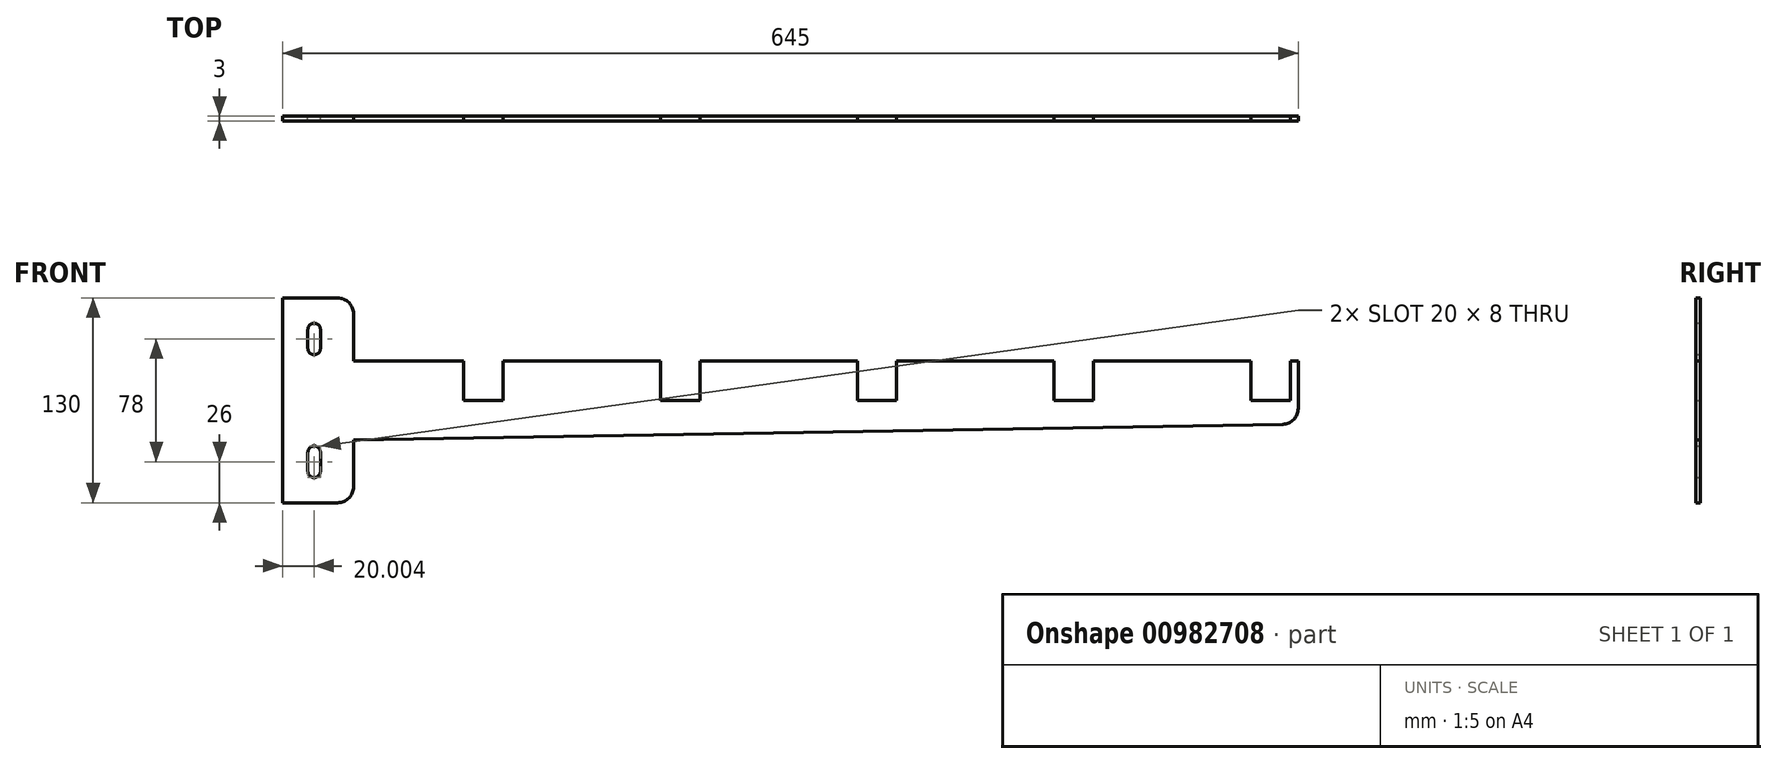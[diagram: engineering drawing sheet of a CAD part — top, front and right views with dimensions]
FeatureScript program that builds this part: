
annotation { "Feature Type Name" : "Feature", "Feature Type Description" : "" }
export const myFeature = defineFeature(function(context is Context, id is Id, definition is map)
    precondition{}
    {
        {
            var Q0;
            Q0=qCreatedBy(makeId("Front.planeOp"),FACE);
            var sketch = newSketch(context, id + "F0", { "sketchPlane" : qUnion([Q0])});
            skLineSegment(sketch, "E0", {"start": v(-171.16, 0) * mm, "end": v(-101.16, 0) * mm});
            skLineSegment(sketch, "E1", {"start": v(428.84, 0) * mm, "end": v(428.84, -30.17) * mm});
            skLineSegment(sketch, "E2", {"start": v(419.01, -40.16) * mm, "end": v(-171.16, -50) * mm});
            skLineSegment(sketch, "E3", {"start": v(-171.16, -50) * mm, "end": v(-171.16, -80) * mm});
            skLineSegment(sketch, "E4", {"start": v(-181.16, -90) * mm, "end": v(-216.16, -90) * mm});
            skLineSegment(sketch, "E5", {"start": v(-216.16, -90) * mm, "end": v(-216.16, 40) * mm});
            skLineSegment(sketch, "E6", {"start": v(-171.16, 30) * mm, "end": v(-171.16, -50) * mm});
            skLineSegment(sketch, "E7", {"start": v(-181.16, 40) * mm, "end": v(-216.16, 40) * mm});
            skLineSegment(sketch, "E8", {"start": v(-76.16, 0) * mm, "end": v(-76.16, -25) * mm});
            skLineSegment(sketch, "E9", {"start": v(-101.16, -25) * mm, "end": v(-76.16, -25) * mm});
            skLineSegment(sketch, "E10", {"start": v(-101.16, -25) * mm, "end": v(-101.16, 0) * mm});
            skLineSegment(sketch, "E11", {"start": v(23.84, 0) * mm, "end": v(23.84, -25) * mm});
            skLineSegment(sketch, "E12", {"start": v(23.84, -25) * mm, "end": v(48.84, -25) * mm});
            skLineSegment(sketch, "E13", {"start": v(48.84, -25) * mm, "end": v(48.84, 0) * mm});
            skLineSegment(sketch, "E14", {"start": v(148.84, 0) * mm, "end": v(148.84, -25) * mm});
            skLineSegment(sketch, "E15", {"start": v(148.84, -25) * mm, "end": v(173.84, -25) * mm});
            skLineSegment(sketch, "E16", {"start": v(173.84, -25) * mm, "end": v(173.84, 0) * mm});
            skLineSegment(sketch, "E17", {"start": v(163.13, -25) * mm, "end": v(173.84, -25) * mm});
            skPoint(sketch, "E18.end.orphan", {"position": v(188.13, 0) * mm});
            skLineSegment(sketch, "E19", {"start": v(273.84, 0) * mm, "end": v(273.84, -25) * mm});
            skLineSegment(sketch, "E20", {"start": v(273.84, -25) * mm, "end": v(298.84, -25) * mm});
            skLineSegment(sketch, "E21", {"start": v(298.84, -25) * mm, "end": v(298.84, 0) * mm});
            skLineSegment(sketch, "E22", {"start": v(398.84, 0) * mm, "end": v(398.84, -25) * mm});
            skLineSegment(sketch, "E23", {"start": v(398.84, -25) * mm, "end": v(423.84, -25) * mm});
            skLineSegment(sketch, "E24", {"start": v(423.84, -25) * mm, "end": v(423.84, 0) * mm});
            skLineSegment(sketch, "E25.trimOffspring", {"start": v(-76.16, 0) * mm, "end": v(23.84, 0) * mm});
            skLineSegment(sketch, "E26.trimOffspring", {"start": v(48.84, 0) * mm, "end": v(148.84, 0) * mm});
            skLineSegment(sketch, "E27.trimOffspring", {"start": v(173.84, 0) * mm, "end": v(273.84, 0) * mm});
            skLineSegment(sketch, "E28.trimOffspring", {"start": v(298.84, 0) * mm, "end": v(398.84, 0) * mm});
            skLineSegment(sketch, "E29.trimOffspring", {"start": v(423.84, 0) * mm, "end": v(428.84, 0) * mm});
            skLineSegment(sketch, "E30", {"start": v(-196.16, -70) * mm, "end": v(-196.16, -58) * mm, "construction": true});
            skLineSegment(sketch, "E31", {"start": v(-196.16, 20) * mm, "end": v(-196.16, 8) * mm, "construction": true});
            skArc(sketch, "E32.0.startCap", {"start": v(-200.16, 20) * mm, "mid": v(-196.16, 24) * mm, "end": v(-192.16, 20) * mm});
            skArc(sketch, "E32.0.endCap", {"start": v(-192.16, 8) * mm, "mid": v(-196.16, 4) * mm, "end": v(-200.16, 8) * mm});
            skLineSegment(sketch, "E32.0.left", {"start": v(-192.16, 20) * mm, "end": v(-192.16, 8) * mm});
            skLineSegment(sketch, "E32.0.right", {"start": v(-200.16, 20) * mm, "end": v(-200.16, 8) * mm});
            skArc(sketch, "E32.1.startCap", {"start": v(-192.16, -70) * mm, "mid": v(-196.16, -74) * mm, "end": v(-200.16, -70) * mm});
            skArc(sketch, "E32.1.endCap", {"start": v(-200.16, -58) * mm, "mid": v(-196.16, -54) * mm, "end": v(-192.16, -58) * mm});
            skLineSegment(sketch, "E32.1.left", {"start": v(-200.16, -70) * mm, "end": v(-200.16, -58) * mm});
            skLineSegment(sketch, "E32.1.right", {"start": v(-192.16, -70) * mm, "end": v(-192.16, -58) * mm});
            skPoint(sketch, "E33.visualSharp", {"position": v(-171.16, 40) * mm});
            skArc(sketch, "E33.filletArc", {"start": v(-171.16, 30) * mm, "mid": v(-174.09, 37.07) * mm, "end": v(-181.16, 40) * mm});
            skPoint(sketch, "E34.visualSharp", {"position": v(-171.16, -90) * mm});
            skArc(sketch, "E34.filletArc", {"start": v(-181.16, -90) * mm, "mid": v(-174.09, -87.07) * mm, "end": v(-171.16, -80) * mm});
            skPoint(sketch, "E35.visualSharp", {"position": v(428.84, -40) * mm});
            skArc(sketch, "E35.filletArc", {"start": v(419.01, -40.16) * mm, "mid": v(425.97, -37.18) * mm, "end": v(428.84, -30.17) * mm});
            skSolve(sketch);
        }
        {
            var Q0;
            Q0 = qSketchRegion(id + "F0", true);
            extrude(context, id + "F1", {"entities" : qUnion([Q0]), "depth" : 3 * mm, "offsetDistance" : 25 * mm});
        }
    });
